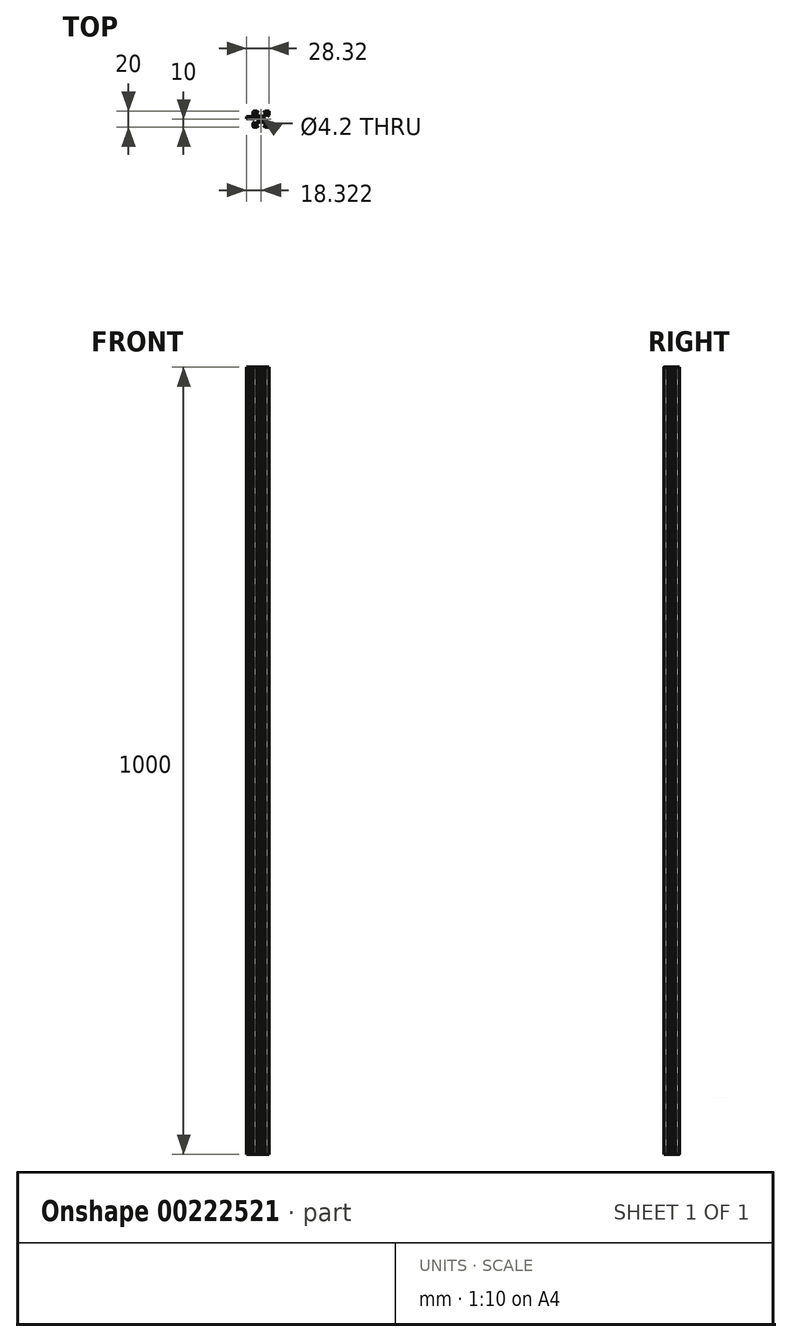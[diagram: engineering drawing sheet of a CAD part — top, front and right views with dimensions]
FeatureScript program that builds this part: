
annotation { "Feature Type Name" : "Feature", "Feature Type Description" : "" }
export const myFeature = defineFeature(function(context is Context, id is Id, definition is map)
    precondition{}
    {
        {
            var Q0;
            Q0=qCreatedBy(makeId("Top.planeOp"),FACE);
            var sketch = newSketch(context, id + "F0", { "sketchPlane" : qUnion([Q0])});
            skArc(sketch, "E0", {"start": v(-28.27, 3.99) * mm, "mid": v(-28.17, 3.92) * mm, "end": v(-28.05, 3.9) * mm});
            skLineSegment(sketch, "E1", {"start": v(-25.44, 3.9) * mm, "end": v(-25.34, 3.7) * mm});
            skCircle(sketch, "E2", {"center": v(-25.34, 0) * mm, "radius": 2.1 * mm});
            skLineSegment(sketch, "E3", {"start": v(-28.27, 3.99) * mm, "end": v(-30.84, 6.56) * mm});
            skLineSegment(sketch, "E4", {"start": v(-30.84, 6.56) * mm, "end": v(-30.84, 7.9) * mm});
            skLineSegment(sketch, "E5", {"start": v(-25.44, 3.9) * mm, "end": v(-28.05, 3.9) * mm});
            skArc(sketch, "E6", {"start": v(-30.54, 8.2) * mm, "mid": v(-30.75, 8.11) * mm, "end": v(-30.84, 7.9) * mm});
            skArc(sketch, "E7", {"start": v(-29.24, 2.72) * mm, "mid": v(-29.26, 2.83) * mm, "end": v(-29.33, 2.93) * mm});
            skLineSegment(sketch, "E8", {"start": v(-29.24, 0.1) * mm, "end": v(-29.04, 0) * mm});
            skLineSegment(sketch, "E9", {"start": v(-29.33, 2.93) * mm, "end": v(-31.9, 5.5) * mm});
            skLineSegment(sketch, "E10", {"start": v(-31.9, 5.5) * mm, "end": v(-33.24, 5.5) * mm});
            skLineSegment(sketch, "E11", {"start": v(-29.24, 0.1) * mm, "end": v(-29.24, 2.72) * mm});
            skArc(sketch, "E12", {"start": v(-33.24, 5.5) * mm, "mid": v(-33.45, 5.41) * mm, "end": v(-33.54, 5.2) * mm});
            skArc(sketch, "E13", {"start": v(-22.62, 3.9) * mm, "mid": v(-22.5, 3.92) * mm, "end": v(-22.41, 3.99) * mm});
            skLineSegment(sketch, "E14", {"start": v(-25.24, 3.9) * mm, "end": v(-25.34, 3.7) * mm});
            skLineSegment(sketch, "E15", {"start": v(-22.41, 3.99) * mm, "end": v(-19.84, 6.56) * mm});
            skLineSegment(sketch, "E16", {"start": v(-19.84, 6.56) * mm, "end": v(-19.84, 7.9) * mm});
            skLineSegment(sketch, "E17", {"start": v(-25.24, 3.9) * mm, "end": v(-22.62, 3.9) * mm});
            skArc(sketch, "E18", {"start": v(-19.84, 7.9) * mm, "mid": v(-19.93, 8.11) * mm, "end": v(-20.14, 8.2) * mm});
            skLineSegment(sketch, "E19", {"start": v(-22.25, 8.2) * mm, "end": v(-20.45, 10) * mm});
            skArc(sketch, "E20", {"start": v(-21.35, 2.93) * mm, "mid": v(-21.41, 2.83) * mm, "end": v(-21.44, 2.72) * mm});
            skLineSegment(sketch, "E21", {"start": v(-21.44, 0.1) * mm, "end": v(-21.64, 0) * mm});
            skLineSegment(sketch, "E22", {"start": v(-21.35, 2.93) * mm, "end": v(-18.78, 5.5) * mm});
            skLineSegment(sketch, "E23", {"start": v(-18.78, 5.5) * mm, "end": v(-17.44, 5.5) * mm});
            skLineSegment(sketch, "E24", {"start": v(-21.44, 0.1) * mm, "end": v(-21.44, 2.72) * mm});
            skArc(sketch, "E25", {"start": v(-17.14, 5.2) * mm, "mid": v(-17.23, 5.41) * mm, "end": v(-17.44, 5.5) * mm});
            skLineSegment(sketch, "E26", {"start": v(-34.94, -10) * mm, "end": v(-30.23, -10) * mm});
            skArc(sketch, "E27", {"start": v(-28.05, -3.9) * mm, "mid": v(-28.17, -3.92) * mm, "end": v(-28.27, -3.99) * mm});
            skLineSegment(sketch, "E28", {"start": v(-25.44, -3.9) * mm, "end": v(-25.34, -3.7) * mm});
            skLineSegment(sketch, "E29", {"start": v(-28.27, -3.99) * mm, "end": v(-30.84, -6.56) * mm});
            skLineSegment(sketch, "E30", {"start": v(-30.84, -6.56) * mm, "end": v(-30.84, -7.9) * mm});
            skLineSegment(sketch, "E31", {"start": v(-25.44, -3.9) * mm, "end": v(-28.05, -3.9) * mm});
            skArc(sketch, "E32", {"start": v(-30.84, -7.9) * mm, "mid": v(-30.75, -8.11) * mm, "end": v(-30.54, -8.2) * mm});
            skLineSegment(sketch, "E33", {"start": v(-35.34, -9.6) * mm, "end": v(-35.34, -4.89) * mm});
            skArc(sketch, "E34", {"start": v(-29.33, -2.93) * mm, "mid": v(-29.26, -2.83) * mm, "end": v(-29.24, -2.72) * mm});
            skLineSegment(sketch, "E35", {"start": v(-29.24, -0.1) * mm, "end": v(-29.04, 0) * mm});
            skLineSegment(sketch, "E36", {"start": v(-29.33, -2.93) * mm, "end": v(-31.9, -5.5) * mm});
            skLineSegment(sketch, "E37", {"start": v(-31.9, -5.5) * mm, "end": v(-33.24, -5.5) * mm});
            skLineSegment(sketch, "E38", {"start": v(-29.24, -0.1) * mm, "end": v(-29.24, -2.72) * mm});
            skArc(sketch, "E39", {"start": v(-33.54, -5.2) * mm, "mid": v(-33.45, -5.41) * mm, "end": v(-33.24, -5.5) * mm});
            skArc(sketch, "E40", {"start": v(-22.41, -3.99) * mm, "mid": v(-22.5, -3.92) * mm, "end": v(-22.62, -3.9) * mm});
            skLineSegment(sketch, "E41", {"start": v(-25.24, -3.9) * mm, "end": v(-25.34, -3.7) * mm});
            skLineSegment(sketch, "E42", {"start": v(-22.41, -3.99) * mm, "end": v(-19.84, -6.56) * mm});
            skLineSegment(sketch, "E43", {"start": v(-19.84, -6.56) * mm, "end": v(-19.84, -7.9) * mm});
            skLineSegment(sketch, "E44", {"start": v(-25.24, -3.9) * mm, "end": v(-22.62, -3.9) * mm});
            skArc(sketch, "E45", {"start": v(-20.14, -8.2) * mm, "mid": v(-19.93, -8.11) * mm, "end": v(-19.84, -7.9) * mm});
            skArc(sketch, "E46", {"start": v(-21.44, -2.72) * mm, "mid": v(-21.41, -2.83) * mm, "end": v(-21.35, -2.93) * mm});
            skLineSegment(sketch, "E47", {"start": v(-21.44, -0.1) * mm, "end": v(-21.64, 0) * mm});
            skLineSegment(sketch, "E48", {"start": v(-21.35, -2.93) * mm, "end": v(-18.78, -5.5) * mm});
            skLineSegment(sketch, "E49", {"start": v(-18.78, -5.5) * mm, "end": v(-17.44, -5.5) * mm});
            skLineSegment(sketch, "E50", {"start": v(-21.44, -0.1) * mm, "end": v(-21.44, -2.72) * mm});
            skArc(sketch, "E51", {"start": v(-17.44, -5.5) * mm, "mid": v(-17.23, -5.41) * mm, "end": v(-17.14, -5.2) * mm});
            skArc(sketch, "E52", {"start": v(-35.34, -9.6) * mm, "mid": v(-35.22, -9.88) * mm, "end": v(-34.94, -10) * mm});
            skLineSegment(sketch, "E53", {"start": v(-34.94, 10) * mm, "end": v(-30.23, 10) * mm});
            skLineSegment(sketch, "E54", {"start": v(-35.34, 9.6) * mm, "end": v(-35.34, 4.89) * mm});
            skArc(sketch, "E55", {"start": v(-34.94, 10) * mm, "mid": v(-35.22, 9.88) * mm, "end": v(-35.34, 9.6) * mm});
            skLineSegment(sketch, "E56", {"start": v(-15.74, -10) * mm, "end": v(-20.45, -10) * mm});
            skLineSegment(sketch, "E57", {"start": v(-15.34, -9.6) * mm, "end": v(-15.34, -4.89) * mm});
            skArc(sketch, "E58", {"start": v(-15.74, -10) * mm, "mid": v(-15.46, -9.88) * mm, "end": v(-15.34, -9.6) * mm});
            skLineSegment(sketch, "E59", {"start": v(-15.74, 10) * mm, "end": v(-20.45, 10) * mm});
            skLineSegment(sketch, "E60", {"start": v(-15.34, 9.6) * mm, "end": v(-15.34, 4.89) * mm});
            skArc(sketch, "E61", {"start": v(-15.34, 9.6) * mm, "mid": v(-15.46, 9.88) * mm, "end": v(-15.74, 10) * mm});
            skLineSegment(sketch, "E62", {"start": v(-30.23, 10) * mm, "end": v(-28.43, 8.2) * mm});
            skLineSegment(sketch, "E63", {"start": v(-28.43, 8.2) * mm, "end": v(-28.73, 8.2) * mm});
            skLineSegment(sketch, "E64", {"start": v(-28.73, 8.2) * mm, "end": v(-30.54, 8.2) * mm});
            skLineSegment(sketch, "E65", {"start": v(-22.25, 8.2) * mm, "end": v(-21.95, 8.2) * mm});
            skLineSegment(sketch, "E66", {"start": v(-21.95, 8.2) * mm, "end": v(-20.14, 8.2) * mm});
            skLineSegment(sketch, "E67", {"start": v(-22.25, -8.2) * mm, "end": v(-20.45, -10) * mm});
            skLineSegment(sketch, "E68", {"start": v(-30.23, -10) * mm, "end": v(-28.43, -8.2) * mm});
            skLineSegment(sketch, "E69", {"start": v(-28.43, -8.2) * mm, "end": v(-28.73, -8.2) * mm});
            skLineSegment(sketch, "E70", {"start": v(-28.73, -8.2) * mm, "end": v(-30.54, -8.2) * mm});
            skLineSegment(sketch, "E71", {"start": v(-22.25, -8.2) * mm, "end": v(-21.95, -8.2) * mm});
            skLineSegment(sketch, "E72", {"start": v(-21.95, -8.2) * mm, "end": v(-20.14, -8.2) * mm});
            skLineSegment(sketch, "E73", {"start": v(-35.34, 4.89) * mm, "end": v(-33.54, 3.09) * mm});
            skLineSegment(sketch, "E74", {"start": v(-33.54, 3.09) * mm, "end": v(-33.54, 3.39) * mm});
            skLineSegment(sketch, "E75", {"start": v(-33.54, 3.39) * mm, "end": v(-33.54, 5.2) * mm});
            skLineSegment(sketch, "E76", {"start": v(-35.34, -4.89) * mm, "end": v(-33.54, -3.09) * mm});
            skLineSegment(sketch, "E77", {"start": v(-33.54, -3.09) * mm, "end": v(-33.54, -3.39) * mm});
            skLineSegment(sketch, "E78", {"start": v(-33.54, -3.39) * mm, "end": v(-33.54, -5.2) * mm});
            skLineSegment(sketch, "E79", {"start": v(-15.34, 4.89) * mm, "end": v(-17.14, 3.09) * mm});
            skLineSegment(sketch, "E80", {"start": v(-17.14, 3.09) * mm, "end": v(-17.14, 3.39) * mm});
            skLineSegment(sketch, "E81", {"start": v(-17.14, 3.39) * mm, "end": v(-17.14, 5.2) * mm});
            skLineSegment(sketch, "E82", {"start": v(-15.34, -4.89) * mm, "end": v(-17.14, -3.09) * mm});
            skLineSegment(sketch, "E83", {"start": v(-17.14, -3.09) * mm, "end": v(-17.14, -3.39) * mm});
            skLineSegment(sketch, "E84", {"start": v(-17.14, -3.39) * mm, "end": v(-17.14, -5.2) * mm});
            skText(sketch, "E85", { "text": "가나다라", "fontName": "OpenSans-Bold.ttf"});
            const initialGuessF0  = {"E85": [-0.04387, 0.0005, 1, 0, 0.00301]};
            skSetInitialGuess(sketch, initialGuessF0);
            skSolve(sketch);
        }
        {
            var Q0;
            Q0 = qSketchRegion(id + "F0", true);
            extrude(context, id + "F1", {"entities" : qUnion([Q0]), "depth" : 1000 * mm});
        }
    });
